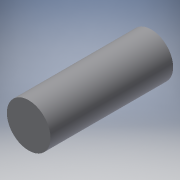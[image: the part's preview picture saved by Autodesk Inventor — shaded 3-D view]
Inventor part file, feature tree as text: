
AUTODESK INVENTOR PART (.ipt)
format: ipt  version: 2018.1 (Build 221171000, 171)  size: 91,648 bytes
history: native  units: mm
features: extrude x1, sketch x1
ambient origin geometry x8: Origin, YZ Plane, XZ Plane, XY Plane, X Axis, Y Axis, Z Axis, Center Point
bodies: Solid1 (feature_tree)
feature tree (2):
  extrude  "Extrusion1"  Depth=50.0mm TaperAngle=0.0deg
  sketch  "Sketch1"  dims[d0=17.8mm d1=50.0mm d2=0.0mm]
